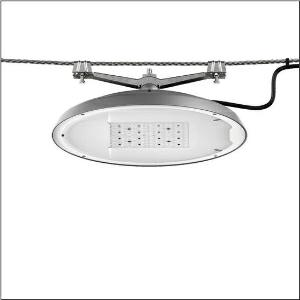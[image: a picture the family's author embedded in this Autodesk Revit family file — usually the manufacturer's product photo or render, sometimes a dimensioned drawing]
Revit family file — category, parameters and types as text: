
# Revit family: dl_r__50_iq_mini___st0_8s_5xa248v41f08le_55a3
name_source: partatom
category: Lighting Fixtures
units: mm (PartAtom-declared; Revit-internal decimal feet)

## family parameters
Cut with Voids When Loaded = No
Host = Face
Light Source = No
Part Type = Normal
Room Calculation Point = No
Round Connector Dimension = Use Diameter
Shared = No

## types (1)
- --- (1 x LED, 10390 lm, 64.1 W, 4000K)
    Apparent Load = 64 VA
    CIE Flux Codes = 38 75 97 100 100
    Color Rendering = 70
    Color Temperature = 4000K
    Default Elevation = 1800 mm
    Description = DL® 50 iQ mini, catenary luminaire, primary light control with lens, of PMMA, primary optical cover: cover, of toughened safety glass, transparent, light distribution: ST0.8s, light emission: direct distribution, primary light characteristic: symmetric, installation type: suspended mounting, LED, High Power LED, rated luminous flux: 10.390lm, luminous efficacy: 162lm/W, light colour: 740, colour temperature: 4000K, control: optimised constant luminous flux control (CLO 2.0), Desk-Remote (wireless, voltage-free reading and setting of iQ features in the workshop via application-optimized NFC function/RFID function), Light-Fading, Smart-Wire, Night-Set, Lumen-Switch, Temp-Guard, Auto-Match, Street-Remote, mains connection: 230..240V, AC, 50/60Hz, start of lifetime: 64W, end of service life: 67W, reduction: 30W, luminaire housing, of diecast aluminium, powder-coated, Siteco® metallic grey (DB 702S), diameter: 500mm, height: 115mm, protection rating (complete): IP66, insulation class (complete): insulation class II (safety insulation), certification: CE, ENEC, VDE, impact resistance: IK08, permissible operating ambient temperature for outdoor applications: -25..+40°C, standard-compliant lighting for roads and squares, packaging unit: 1 piece

Light Distribution: ST0.8s
    Height = 124 mm  [stored 0.406824 ft]
    Lamp = 1 x LED
    Lamp Light Flux = 10390 lm
    Lamp Power = 64.1 W
    Lamp count = 1
    Length = 500 mm
    Luminous efficacy = 162 lm/W
    Manufacturer = Siteco
    ModVariant = No
    Model = 5XA248V41F08LE
    Number of Poles = 1
    OnlyDefault = Yes
    Power Factor = 1
    Product Name = DL® 50 iQ mini | ST0.8s
    Product group = catenary luminaire
    ProductGroupID = 6300
    Protection Class = Protection class II
    Protection Degree = IP 66
    RLX_Detail_Level = 1
    RLX_Emergency_Light_Flux = 0 lm
    RLX_Emergency_Type = 0
    RLX_Emergency_Type_DB = No
    RlxData = <blob elided: 126917 chars, md5=5665be85>
    Socket = socket
    Standby Power = 0 W
    System Light Flux = 10390 lm
    System Power = 64 W
    Type Comments = factory setting: luminous flux: 100 % | dim-lin: 254 | 672 mA
    Type Image = l_1251783.jpg
    URL = http://relux.com
    VarID = @adj_072345
    Voltage = 0 V
    Weight = 0.00 kg
    Width = 0 mm  [stored 0 ft]

note: [stored X ft] marks values corroborated as IEEE doubles in the binary element streams (Revit-internal decimal feet)

## geometry (parser evidence)
native form markers: Blend x4, Sweep x14
no freeform markers — native parametric forms only
